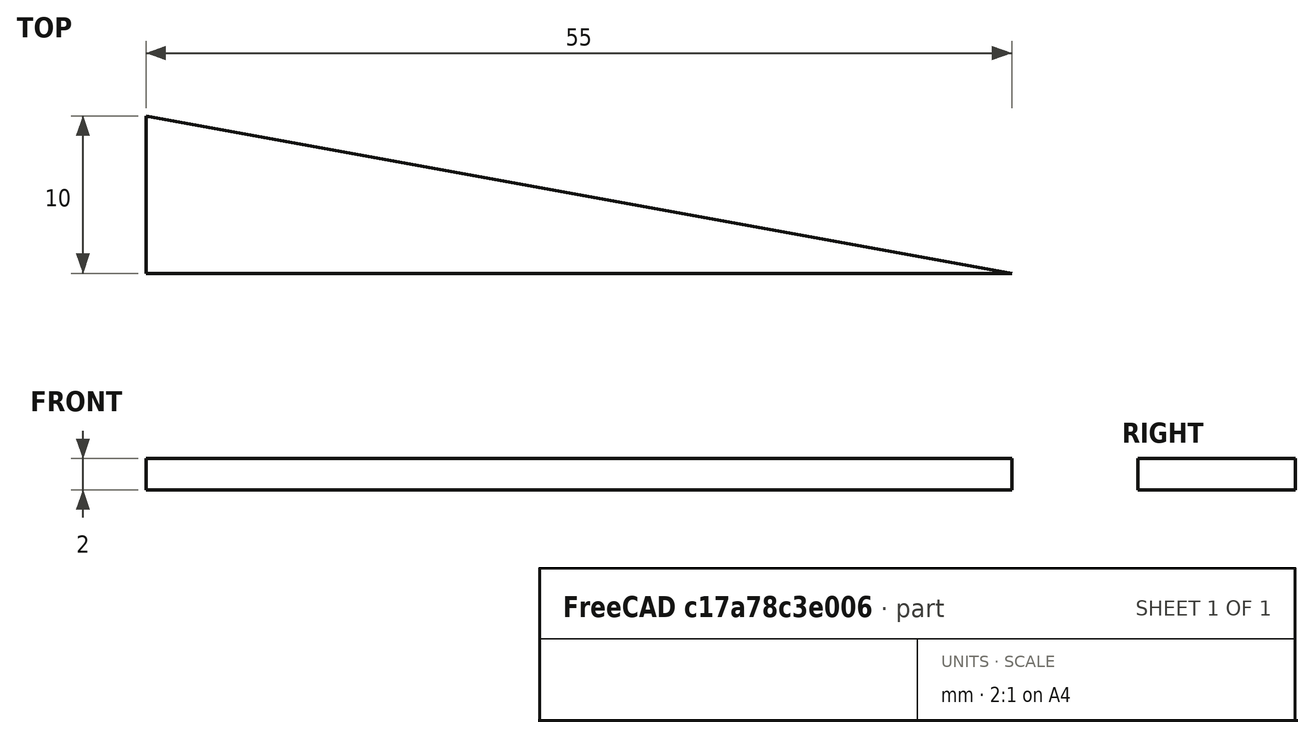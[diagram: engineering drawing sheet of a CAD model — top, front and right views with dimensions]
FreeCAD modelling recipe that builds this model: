
FCSTD DOCUMENT  (FreeCAD 0.20R29410 (Git))
Label: wedge
License: All rights reserved
LicenseURL: http://en.wikipedia.org/wiki/All_rights_reserved
objects: Sketcher::SketchObject×1, PartDesign::Pad×1, PartDesign::Body×1, App::Part×1
note: 4 computed .brp shape members not serialized (recipe doc carries the construction recipe); baked Part::Feature solids carry a one-line shape summary decoded from their .brp

FEATURE [Sketcher::SketchObject] Sketch
  FullyConstrained = true
  MapMode = 5
  Support = -> [XY_Plane001]
  sketch-geometry (3):
    g0: LineSegment StartX=0 StartY=0 StartZ=0 EndX=55 EndY=0 EndZ=0
    g1: LineSegment StartX=0 StartY=10 StartZ=0 EndX=0 EndY=0 EndZ=0
    g2: LineSegment StartX=0 StartY=10 StartZ=0 EndX=55 EndY=0 EndZ=0
  constraints (8):
    c: Horizontal(g0)
    c: Coincident(g1,g2)
    c: Coincident(g1,g-1)
    c: Coincident(g0,g1)
    c: Coincident(g2,g0)
    c: Vertical(g1)
    c: Distance(g0) = 55
    c: Distance(g1) = 10
FEATURE [PartDesign::Pad] Pad
  Direction = (0,0,1)
  Length = 2
  Length2 = 10
  Profile = -> Sketch
  ReferenceAxis = -> Sketch [N_Axis]
  Type = 0
FEATURE [PartDesign::Body] Body
  Group = -> [Sketch,Pad]
  Origin = -> Origin001
  Tip = -> Pad
FEATURE [App::Part] Part
  Group = -> [Body]
  Origin = -> Origin
